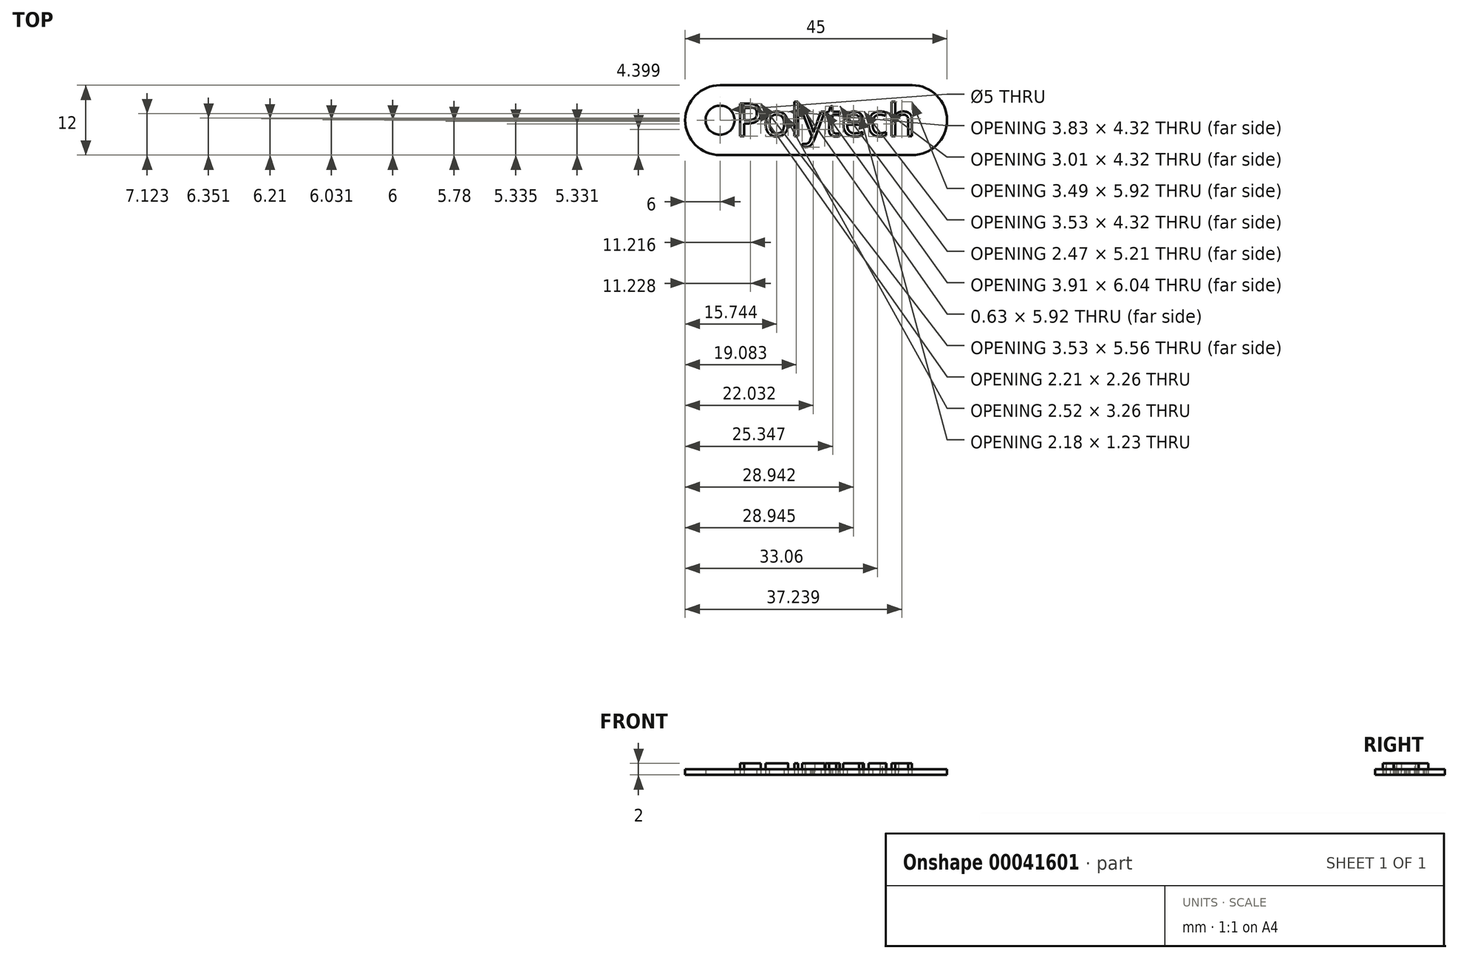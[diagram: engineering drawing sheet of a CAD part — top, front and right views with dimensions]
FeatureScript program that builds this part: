
annotation { "Feature Type Name" : "Feature", "Feature Type Description" : "" }
export const myFeature = defineFeature(function(context is Context, id is Id, definition is map)
    precondition{}
    {
        {
            var Q0;
            Q0=qCreatedBy(makeId("Top.planeOp"),FACE);
            var sketch = newSketch(context, id + "F0", { "sketchPlane" : qUnion([Q0])});
            skLineSegment(sketch, "E0.rect.bottom", {"start": v(16.5, 6) * mm, "end": v(-16.5, 6) * mm});
            skLineSegment(sketch, "E0.rect.top", {"start": v(16.5, -6) * mm, "end": v(-16.5, -6) * mm});
            skLineSegment(sketch, "E0.rect.left", {"start": v(16.5, 6) * mm, "end": v(16.5, -6) * mm});
            skLineSegment(sketch, "E0.rect.right", {"start": v(-16.5, 6) * mm, "end": v(-16.5, -6) * mm});
            skPoint(sketch, "E0.rect.middle", {"position": v(0, 0) * mm});
            skArc(sketch, "E1", {"start": v(-16.5, 6) * mm, "mid": v(-22.5, 0) * mm, "end": v(-16.5, -6) * mm});
            skArc(sketch, "E2", {"start": v(16.5, -6) * mm, "mid": v(22.5, 0) * mm, "end": v(16.5, 6) * mm});
            skCircle(sketch, "E3", {"center": v(-16.5, 0) * mm, "radius": 2.5 * mm});
            skText(sketch, "E4", { "text": "Polytech", "fontName": "OpenSans-Regular.ttf"});
            const initialGuessF0  = {"E4": [-0.0138, -0.00275, 1, 0, 0.00561]};
            skSetInitialGuess(sketch, initialGuessF0);
            skSolve(sketch);
        }
        {
            var Q0;
            Q0=makeQuery(id+"F0.imprint","IMPRINT",FACE,{"disambiguationData":[TD([[makeQuery(id+"F0.imprint","IMPRINT",EDGE,{"derivedFrom":sQuery(id+"F0.wireOp",EDGE,"E4.sketch_text.stroke-0")}),-1.0]])]});
            var Q1;
            Q1=makeQuery(id+"F0.imprint","IMPRINT",FACE,{"disambiguationData":[TD([[makeQuery(id+"F0.imprint","IMPRINT",EDGE,{"derivedFrom":sQuery(id+"F0.wireOp",EDGE,"E4.sketch_text.stroke-15")}),-1.0]])]});
            var Q2;
            Q2=makeQuery(id+"F0.imprint","IMPRINT",FACE,{"disambiguationData":[TD([[makeQuery(id+"F0.imprint","IMPRINT",EDGE,{"derivedFrom":sQuery(id+"F0.wireOp",EDGE,"E4.sketch_text.stroke-105")}),-1.0]])]});
            var Q3;
            Q3=makeQuery(id+"F0.imprint","IMPRINT",FACE,{"disambiguationData":[TD([[makeQuery(id+"F0.imprint","IMPRINT",EDGE,{"derivedFrom":sQuery(id+"F0.wireOp",EDGE,"E4.sketch_text.stroke-90")}),-1.0]])]});
            var Q4;
            Q4=makeQuery(id+"F0.imprint","IMPRINT",FACE,{"disambiguationData":[TD([[makeQuery(id+"F0.imprint","IMPRINT",EDGE,{"derivedFrom":sQuery(id+"F0.wireOp",EDGE,"E4.sketch_text.stroke-71")}),-1.0]])]});
            var Q5;
            Q5=makeQuery(id+"F0.imprint","IMPRINT",FACE,{"disambiguationData":[TD([[makeQuery(id+"F0.imprint","IMPRINT",EDGE,{"derivedFrom":sQuery(id+"F0.wireOp",EDGE,"E4.sketch_text.stroke-52")}),-1.0]])]});
            var Q6;
            Q6=makeQuery(id+"F0.imprint","IMPRINT",FACE,{"disambiguationData":[TD([[makeQuery(id+"F0.imprint","IMPRINT",EDGE,{"derivedFrom":sQuery(id+"F0.wireOp",EDGE,"E4.sketch_text.stroke-36")}),-1.0]])]});
            var Q7;
            Q7=makeQuery(id+"F0.imprint","IMPRINT",FACE,{"disambiguationData":[TD([[makeQuery(id+"F0.imprint","IMPRINT",EDGE,{"derivedFrom":sQuery(id+"F0.wireOp",EDGE,"E4.sketch_text.stroke-32")}),-1.0]])]});
            extrude(context, id + "F1", {"entities" : qUnion([Q0, Q1, Q2, Q3, Q4, Q5, Q6, Q7]), "depth" : 2 * mm, "offsetDistance" : 25 * mm});
        }
        {
            var Q0;
            Q0 = qSketchRegion(id + "F0", true);
            var Q1;
            Q1=makeQuery(id+"F0.imprint","IMPRINT",FACE,{"disambiguationData":[TD([[makeQuery(id+"F0.imprint","IMPRINT",EDGE,{"derivedFrom":sQuery(id+"F0.wireOp",EDGE,"E4.sketch_text.stroke-8")}),1.0]])]});
            var Q2;
            Q2=makeQuery(id+"F0.imprint","IMPRINT",FACE,{"disambiguationData":[TD([[makeQuery(id+"F0.imprint","IMPRINT",EDGE,{"derivedFrom":sQuery(id+"F0.wireOp",EDGE,"E4.sketch_text.stroke-24")}),1.0]])]});
            var Q3;
            Q3=makeQuery(id+"F0.imprint","IMPRINT",FACE,{"disambiguationData":[TD([[makeQuery(id+"F0.imprint","IMPRINT",EDGE,{"derivedFrom":sQuery(id+"F0.wireOp",EDGE,"E4.sketch_text.stroke-85")}),1.0]])]});
            extrude(context, id + "F2", {"entities" : qUnion([Q0, Q1, Q2, Q3]), "depth" : 1 * mm});
        }
    });
